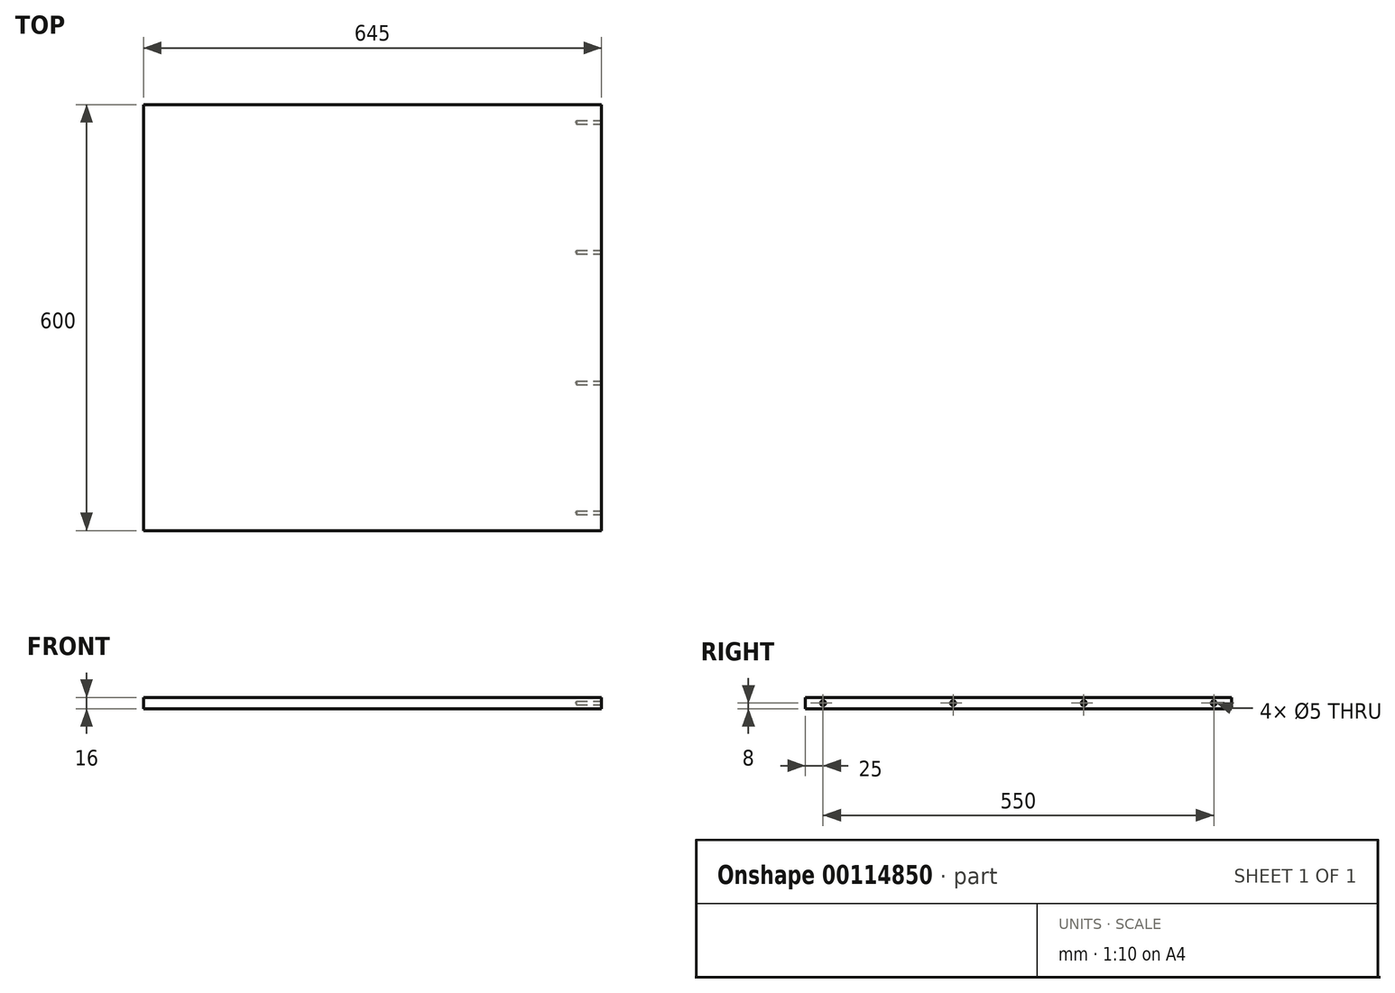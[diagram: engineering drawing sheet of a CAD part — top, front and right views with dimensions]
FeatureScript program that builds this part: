
annotation { "Feature Type Name" : "Feature", "Feature Type Description" : "" }
export const myFeature = defineFeature(function(context is Context, id is Id, definition is map)
    precondition{}
    {
        {
            var Q0;
            Q0=qCreatedBy(makeId("Top.planeOp"),FACE);
            var sketch = newSketch(context, id + "F0", { "sketchPlane" : qUnion([Q0])});
            skLineSegment(sketch, "E0.bottom", {"start": v(-322.5, 300) * mm, "end": v(322.5, 300) * mm});
            skLineSegment(sketch, "E0.top", {"start": v(-322.5, -300) * mm, "end": v(322.5, -300) * mm});
            skLineSegment(sketch, "E0.left", {"start": v(-322.5, 300) * mm, "end": v(-322.5, -300) * mm});
            skLineSegment(sketch, "E0.right", {"start": v(322.5, 300) * mm, "end": v(322.5, -300) * mm});
            skPoint(sketch, "E0.middle", {"position": v(0, 0) * mm});
            skSolve(sketch);
        }
        {
            var Q0;
            Q0=makeQuery(id+"F0.imprint","IMPRINT",FACE,{"disambiguationData":[TD([[makeQuery(id+"F0.imprint","IMPRINT",EDGE,{"derivedFrom":sQuery(id+"F0.wireOp",EDGE,"E0.bottom")}),-1.0]])]});
            extrude(context, id + "F1", {"entities" : qUnion([Q0]), "endBound" : BoundingType.SYMMETRIC, "depth" : 16 * mm});
        }
        {
            var Q0;
            Q0=makeQuery(id+"F1.opExtrude","SWEPT_FACE",FACE,{"disambiguationData":[OSD([sQuery(id+"F0.wireOp",EDGE,"E0.right")])]});
            var sketch = newSketch(context, id + "F2", { "sketchPlane" : qUnion([Q0])});
            skPoint(sketch, "E1", {"position": v(-275, 0) * mm});
            skPoint(sketch, "E2", {"position": v(-92, 0) * mm});
            skPoint(sketch, "E3", {"position": v(92, 0) * mm});
            skPoint(sketch, "E4", {"position": v(275, 0) * mm});
            skSolve(sketch);
        }
        {
            var Q0;
            Q0=sQuery(id+"F2.wireOp",VERTEX,"E1");
            var Q1;
            Q1=sQuery(id+"F2.wireOp",VERTEX,"E2");
            var Q2;
            Q2=sQuery(id+"F2.wireOp",VERTEX,"E3");
            var Q3;
            Q3=sQuery(id+"F2.wireOp",VERTEX,"E4");
            var Q4;
            Q4=makeQuery(id+"F1.opExtrude","SWEPT_BODY",BODY,{"disambiguationData":[OSD([sQuery(id+"F0.wireOp",EDGE,"E0.bottom"),sQuery(id+"F0.wireOp",EDGE,"E0.top"),sQuery(id+"F0.wireOp",EDGE,"E0.left"),sQuery(id+"F0.wireOp",EDGE,"E0.right")])]});
            hole(context, id + "F3", {"style" : HoleStyle.C_SINK, "endStyle" : HoleEndStyle.BLIND, "holeDiameter" : 5 * mm, "cSinkDiameter" : 7 * mm, "cSinkAngle" : 90 * degree, "holeDepth" : 35 * mm, "locations" : qUnion([Q0, Q1, Q2, Q3]), "scope" : qUnion([Q4])});
        }
    });
